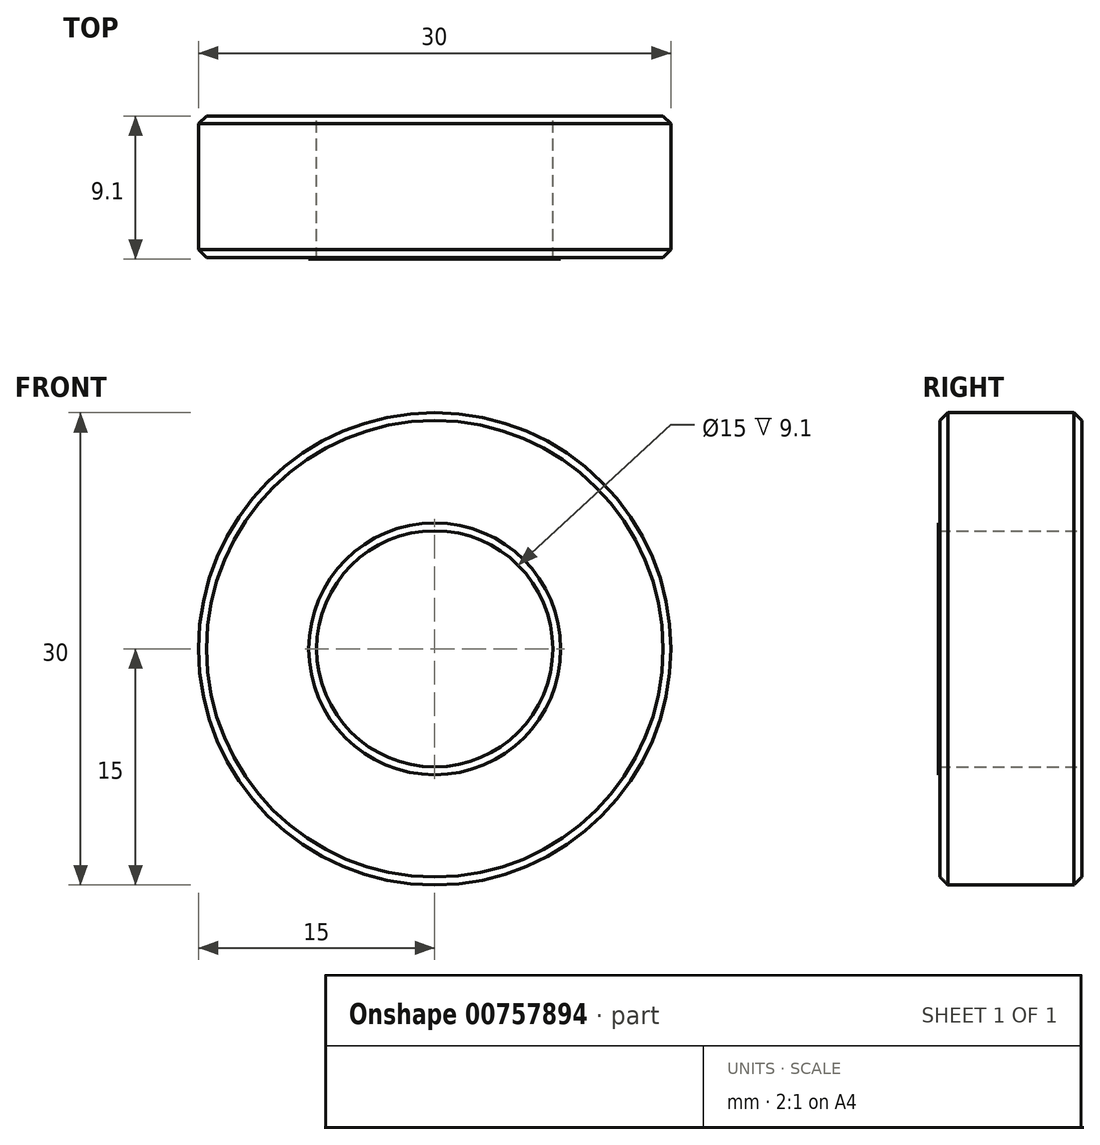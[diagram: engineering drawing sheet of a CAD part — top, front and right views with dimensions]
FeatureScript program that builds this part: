
annotation { "Feature Type Name" : "Feature", "Feature Type Description" : "" }
export const myFeature = defineFeature(function(context is Context, id is Id, definition is map)
    precondition{}
    {
        {
            var Q0;
            Q0=qCreatedBy(makeId("Front.planeOp"),FACE);
            var sketch = newSketch(context, id + "F0", { "sketchPlane" : qUnion([Q0])});
            skCircle(sketch, "E0", {"center": v(0, 0) * mm, "radius": 15 * mm});
            skCircle(sketch, "E1", {"center": v(0, 0) * mm, "radius": 7.5 * mm});
            skSolve(sketch);
        }
        {
            var Q0;
            Q0 = qSketchRegion(id + "F0", true);
            extrude(context, id + "F1", {"entities" : qUnion([Q0]), "depth" : 9 * mm, "offsetDistance" : 25 * mm});
        }
        {
            var Q0;
            Q0=makeQuery(id+"F1.opExtrude","CAP_EDGE",EDGE,{"disambiguationData":[OSD([sQuery(id+"F0.wireOp",EDGE,"E0")])],"isStart":false});
            var Q1;
            Q1=makeQuery(id+"F1.opExtrude","SWEPT_FACE",FACE,{"disambiguationData":[OSD([sQuery(id+"F0.wireOp",EDGE,"E0")])]});
            chamfer(context, id + "F2", {"entities" : qUnion([Q0, Q1]), "width" : .5 * mm, "tangentPropagation" : true});
        }
        {
            var Q0;
            Q0=makeQuery(id+"F1.opExtrude","CAP_FACE",FACE,{"disambiguationData":[OSD([sQuery(id+"F0.wireOp",EDGE,"E0"),sQuery(id+"F0.wireOp",EDGE,"E1")])],"isStart":false});
            var sketch = newSketch(context, id + "F3", { "sketchPlane" : qUnion([Q0])});
            skCircle(sketch, "E2", {"center": v(0, 0) * mm, "radius": 8 * mm});
            skSolve(sketch);
        }
        {
            var Q0;
            Q0=makeQuery(id+"F3.imprint","IMPRINT",FACE,{"disambiguationData":[TD([[makeQuery(id+"F3.imprint","IMPRINT",EDGE,{"derivedFrom":sQuery(id+"F3.wireOp",EDGE,"E2")}),1.0]])]});
            extrude(context, id + "F4", {"entities" : qUnion([Q0]), "operationType" : NewBodyOperationType.ADD, "depth" : .1 * mm, "offsetDistance" : 25 * mm});
        }
    });
